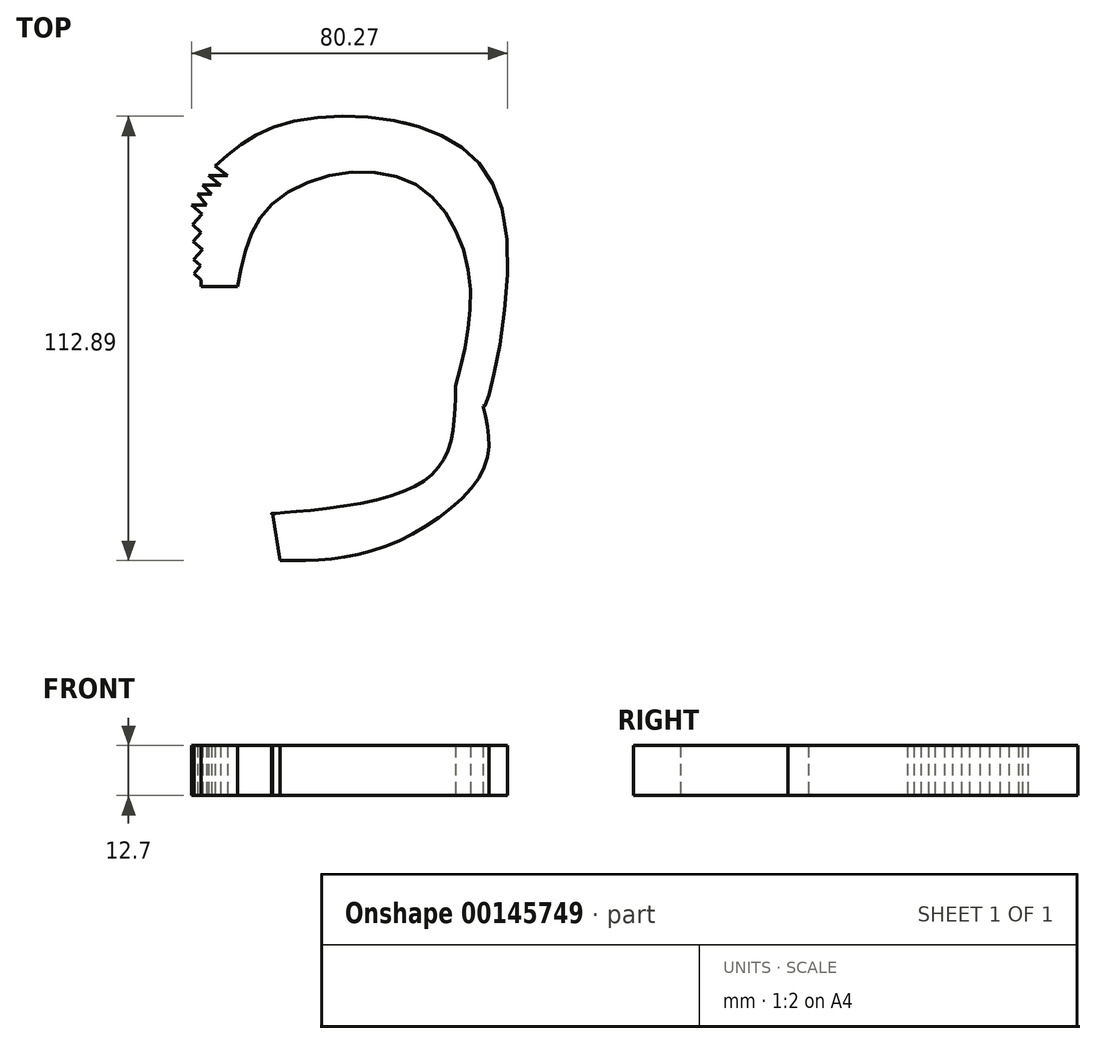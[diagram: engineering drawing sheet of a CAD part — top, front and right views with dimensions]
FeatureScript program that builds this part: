
annotation { "Feature Type Name" : "Feature", "Feature Type Description" : "" }
export const myFeature = defineFeature(function(context is Context, id is Id, definition is map)
    precondition{}
    {
        {
            var Q0;
            Q0=qCreatedBy(makeId("Top.planeOp"),FACE);
            var sketch = newSketch(context, id + "F0", { "sketchPlane" : qUnion([Q0])});
            skFitSpline(sketch, "E0", {"points": [v(-37.75, -12.8) * mm, v(-28.03, 9.06) * mm, v(5.23, 14.28) * mm, v(21.1, -9.99) * mm, v(17.66, -38.02) * mm], "startDerivative": vector(19.98, 106.91) * mm, "endDerivative": vector(-29.24, -111.14) * mm});
            skLineSegment(sketch, "E1", {"start": v(-37.75, -12.8) * mm, "end": v(-46.9, -12.8) * mm});
            skLineSegment(sketch, "E2", {"start": v(-46.9, -12.8) * mm, "end": v(-46.9, -11.14) * mm});
            skLineSegment(sketch, "E3", {"start": v(-46.9, -11.14) * mm, "end": v(-48.77, -9.46) * mm});
            skLineSegment(sketch, "E4", {"start": v(-48.77, -9.46) * mm, "end": v(-47.03, -7.51) * mm});
            skLineSegment(sketch, "E5", {"start": v(-47.03, -7.51) * mm, "end": v(-48.83, -5.9) * mm});
            skLineSegment(sketch, "E6", {"start": v(-48.83, -5.9) * mm, "end": v(-46.64, -3.45) * mm});
            skLineSegment(sketch, "E7", {"start": v(-46.64, -3.45) * mm, "end": v(-48.96, -1.37) * mm});
            skLineSegment(sketch, "E8", {"start": v(-48.96, -1.37) * mm, "end": v(-46.91, 0.92) * mm});
            skLineSegment(sketch, "E9", {"start": v(-46.91, 0.92) * mm, "end": v(-49.13, 2.91) * mm});
            skLineSegment(sketch, "E10", {"start": v(-49.13, 2.91) * mm, "end": v(-46.72, 5.59) * mm});
            skLineSegment(sketch, "E11", {"start": v(-46.72, 5.59) * mm, "end": v(-49.38, 7.97) * mm});
            skLineSegment(sketch, "E12", {"start": v(-49.38, 7.97) * mm, "end": v(-45.6, 7.97) * mm});
            skLineSegment(sketch, "E13", {"start": v(-45.6, 7.97) * mm, "end": v(-47.84, 10.72) * mm});
            skLineSegment(sketch, "E14", {"start": v(-47.84, 10.72) * mm, "end": v(-44.29, 10.72) * mm});
            skLineSegment(sketch, "E15", {"start": v(-44.29, 10.72) * mm, "end": v(-46.53, 12.96) * mm});
            skLineSegment(sketch, "E16", {"start": v(-46.53, 12.96) * mm, "end": v(-42.05, 12.96) * mm});
            skLineSegment(sketch, "E17", {"start": v(-42.05, 12.96) * mm, "end": v(-45.04, 15.39) * mm});
            skLineSegment(sketch, "E18", {"start": v(-45.04, 15.39) * mm, "end": v(-40.18, 15.39) * mm});
            skLineSegment(sketch, "E19", {"start": v(-40.18, 15.39) * mm, "end": v(-43.35, 17.82) * mm});
            skFitSpline(sketch, "E20", {"points": [v(-43.35, 17.82) * mm, v(-27.82, 27.95) * mm, v(7.54, 28.03) * mm, v(30.15, 3.96) * mm, v(25.17, -43) * mm, v(24.88, -43.16) * mm, v(24.7, -43.16) * mm], "startDerivative": vector(71.9, 64.61) * mm, "endDerivative": vector(-10.57, -1.53) * mm});
            skFitSpline(sketch, "E21", {"points": [v(24.7, -43.16) * mm, v(24.7, -59.37) * mm, v(0, -78.79) * mm, v(-26.88, -82.43) * mm], "startDerivative": vector(14.12, -59.2) * mm, "endDerivative": vector(-74.54, -0.3) * mm});
            skFitSpline(sketch, "E22", {"points": [v(17.66, -38.02) * mm, v(14.86, -56.34) * mm, v(-2.77, -67.09) * mm, v(-29.06, -70.51) * mm, v(-28.86, -70.5) * mm], "startDerivative": vector(-1.03, -67.21) * mm, "endDerivative": vector(10.33, 0.33) * mm});
            skLineSegment(sketch, "E23", {"start": v(-28.86, -70.5) * mm, "end": v(-26.88, -82.43) * mm});
            skSolve(sketch);
        }
        {
            var Q0;
            Q0=makeQuery(id+"F0.imprint","IMPRINT",FACE,{"disambiguationData":[TD([[makeQuery(id+"F0.imprint","IMPRINT",EDGE,{"derivedFrom":sQuery(id+"F0.wireOp",EDGE,"E0")}),1.0]])]});
            extrude(context, id + "F1", {"entities" : qUnion([Q0]), "depth" : 12.7 * mm});
        }
    });
